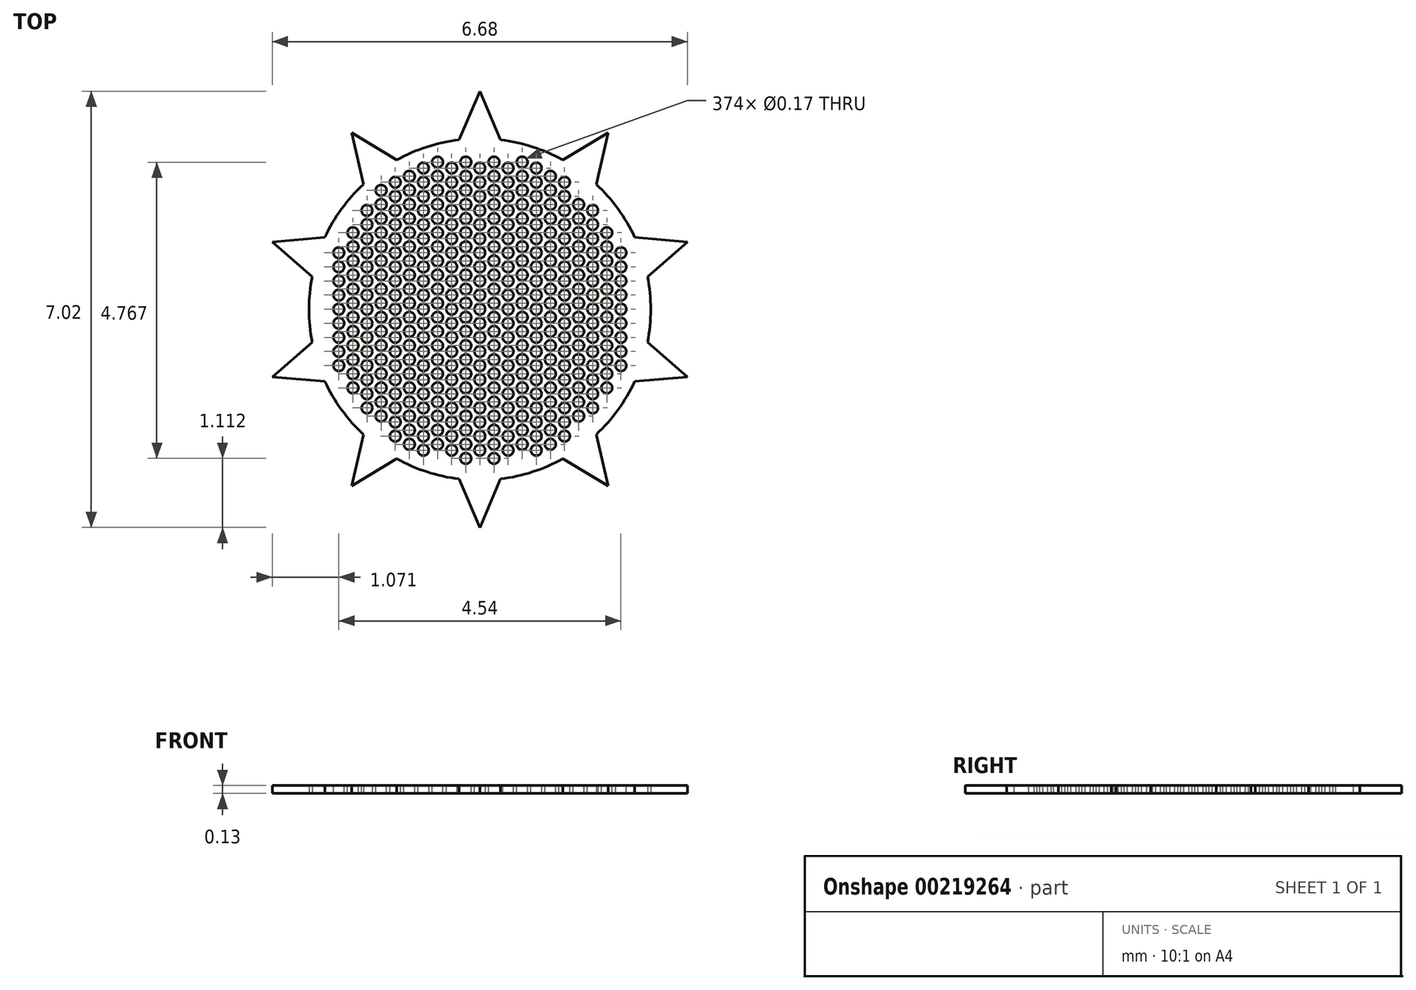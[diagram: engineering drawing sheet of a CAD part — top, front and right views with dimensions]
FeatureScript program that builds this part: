
annotation { "Feature Type Name" : "Feature", "Feature Type Description" : "" }
export const myFeature = defineFeature(function(context is Context, id is Id, definition is map)
    precondition{}
    {
        {
            var Q0;
            Q0=qCreatedBy(makeId("Top.planeOp"),FACE);
            var sketch = newSketch(context, id + "F0", { "sketchPlane" : qUnion([Q0])});
            skCircle(sketch, "E0", {"center": v(0, 0) * mm, "radius": 2.5 * mm});
            skCircle(sketch, "E1", {"center": v(0, 0) * mm, "radius": 2.75 * mm});
            skPoint(sketch, "E2", {"position": v(0, 2.75) * mm});
            skLineSegment(sketch, "E3", {"start": v(-3.94, 3.51) * mm, "end": v(3.7, 3.51) * mm, "construction": true});
            skLineSegment(sketch, "E4", {"start": v(0, 3.51) * mm, "end": v(-0.33, 2.73) * mm});
            skLineSegment(sketch, "E5", {"start": v(0, 3.51) * mm, "end": v(0.33, 2.73) * mm});
            skLineSegment(sketch, "E6.1.0", {"start": v(-2.06, 2.84) * mm, "end": v(-1.87, 2.01) * mm});
            skLineSegment(sketch, "E6.1.1", {"start": v(-2.06, 2.84) * mm, "end": v(-1.34, 2.4) * mm});
            skLineSegment(sketch, "E6.2.0", {"start": v(-3.34, 1.09) * mm, "end": v(-2.7, 0.53) * mm});
            skLineSegment(sketch, "E6.2.1", {"start": v(-3.34, 1.09) * mm, "end": v(-2.5, 1.16) * mm});
            skLineSegment(sketch, "E6.3.0", {"start": v(-3.34, -1.09) * mm, "end": v(-2.5, -1.16) * mm});
            skLineSegment(sketch, "E6.3.1", {"start": v(-3.34, -1.09) * mm, "end": v(-2.7, -0.53) * mm});
            skLineSegment(sketch, "E6.4.0", {"start": v(-2.06, -2.84) * mm, "end": v(-1.34, -2.4) * mm});
            skLineSegment(sketch, "E6.4.1", {"start": v(-2.06, -2.84) * mm, "end": v(-1.87, -2.01) * mm});
            skLineSegment(sketch, "E6.5.0", {"start": v(0, -3.51) * mm, "end": v(0.33, -2.73) * mm});
            skLineSegment(sketch, "E6.5.1", {"start": v(0, -3.51) * mm, "end": v(-0.33, -2.73) * mm});
            skLineSegment(sketch, "E6.6.0", {"start": v(2.06, -2.84) * mm, "end": v(1.87, -2.01) * mm});
            skLineSegment(sketch, "E6.6.1", {"start": v(2.06, -2.84) * mm, "end": v(1.34, -2.4) * mm});
            skLineSegment(sketch, "E6.7.0", {"start": v(3.34, -1.09) * mm, "end": v(2.7, -0.53) * mm});
            skLineSegment(sketch, "E6.7.1", {"start": v(3.34, -1.09) * mm, "end": v(2.5, -1.16) * mm});
            skLineSegment(sketch, "E6.8.0", {"start": v(3.34, 1.09) * mm, "end": v(2.5, 1.16) * mm});
            skLineSegment(sketch, "E6.8.1", {"start": v(3.34, 1.09) * mm, "end": v(2.7, 0.53) * mm});
            skLineSegment(sketch, "E6.9.0", {"start": v(2.06, 2.84) * mm, "end": v(1.34, 2.4) * mm});
            skLineSegment(sketch, "E6.9.1", {"start": v(2.06, 2.84) * mm, "end": v(1.87, 2.01) * mm});
            skSolve(sketch);
        }
        {
            var Q0;
            Q0=qSketchRegion(id+"F0",true);
            var Q1;
            Q1=makeQuery(id+"F0.imprint","IMPRINT",FACE,{"disambiguationData":[TD([[makeQuery(id+"F0.imprint","IMPRINT",EDGE,{"derivedFrom":sQuery(id+"F0.wireOp",EDGE,"E0")}),1.0]])]});
            extrude(context, id + "F1", {"entities" : qUnion([Q0, Q1]), "depth" : 0.13 * mm});
        }
        {
            var Q0;
            Q0=makeQuery(id+"F1.opExtrude","CAP_FACE",FACE,{"disambiguationData":[OSD([sQuery(id+"F0.wireOp",EDGE,"E1"),sQuery(id+"F0.wireOp",EDGE,"E4"),sQuery(id+"F0.wireOp",EDGE,"E5"),sQuery(id+"F0.wireOp",EDGE,"E6.1.0"),sQuery(id+"F0.wireOp",EDGE,"E6.1.1"),sQuery(id+"F0.wireOp",EDGE,"E6.2.0"),sQuery(id+"F0.wireOp",EDGE,"E6.2.1"),sQuery(id+"F0.wireOp",EDGE,"E6.3.0"),sQuery(id+"F0.wireOp",EDGE,"E6.3.1"),sQuery(id+"F0.wireOp",EDGE,"E6.4.0"),sQuery(id+"F0.wireOp",EDGE,"E6.4.1"),sQuery(id+"F0.wireOp",EDGE,"E6.5.0"),sQuery(id+"F0.wireOp",EDGE,"E6.5.1"),sQuery(id+"F0.wireOp",EDGE,"E6.6.0"),sQuery(id+"F0.wireOp",EDGE,"E6.6.1"),sQuery(id+"F0.wireOp",EDGE,"E6.7.0"),sQuery(id+"F0.wireOp",EDGE,"E6.7.1"),sQuery(id+"F0.wireOp",EDGE,"E6.8.0"),sQuery(id+"F0.wireOp",EDGE,"E6.8.1"),sQuery(id+"F0.wireOp",EDGE,"E6.9.0"),sQuery(id+"F0.wireOp",EDGE,"E6.9.1")])],"isStart":false});
            cPlane(context, id + "F2", {"entities" : qUnion([Q0]), "cplaneType" : CPlaneType.OFFSET, "offset" : 0 * mm, "width" : 150 * mm, "height" : 150 * mm});
        }
        {
            var Q0;
            Q0=qCreatedBy(id+"F2.planeOp",FACE);
            var sketch = newSketch(context, id + "F3", { "sketchPlane" : qUnion([Q0])});
            skCircle(sketch, "E7.2.1.8", {"center": v(-2.04, 1.23) * mm, "radius": 0.09 * mm});
            skCircle(sketch, "E7.2.1.9", {"center": v(-2.04, 1) * mm, "radius": 0.09 * mm});
            skCircle(sketch, "E7.0.1.10", {"center": v(-2.27, 0.91) * mm, "radius": 0.09 * mm});
            skCircle(sketch, "E7.2.1.10", {"center": v(-2.04, 0.78) * mm, "radius": 0.09 * mm});
            skCircle(sketch, "E7.2.2.5", {"center": v(-1.59, 1.91) * mm, "radius": 0.09 * mm});
            skCircle(sketch, "E7.2.2.6", {"center": v(-1.59, 1.69) * mm, "radius": 0.09 * mm});
            skCircle(sketch, "E7.0.2.7", {"center": v(-1.82, 1.6) * mm, "radius": 0.09 * mm});
            skCircle(sketch, "E7.2.2.7", {"center": v(-1.59, 1.46) * mm, "radius": 0.09 * mm});
            skCircle(sketch, "E7.0.2.8", {"center": v(-1.82, 1.36) * mm, "radius": 0.09 * mm});
            skCircle(sketch, "E7.2.2.8", {"center": v(-1.59, 1.23) * mm, "radius": 0.09 * mm});
            skCircle(sketch, "E7.0.2.9", {"center": v(-1.82, 1.14) * mm, "radius": 0.09 * mm});
            skCircle(sketch, "E7.2.2.9", {"center": v(-1.59, 1) * mm, "radius": 0.09 * mm});
            skCircle(sketch, "E7.0.2.10", {"center": v(-1.82, 0.91) * mm, "radius": 0.09 * mm});
            skCircle(sketch, "E7.2.2.10", {"center": v(-1.59, 0.78) * mm, "radius": 0.09 * mm});
            skCircle(sketch, "E7.2.3.4", {"center": v(-1.13, 2.14) * mm, "radius": 0.09 * mm});
            skCircle(sketch, "E7.0.3.5", {"center": v(-1.36, 2.05) * mm, "radius": 0.09 * mm});
            skCircle(sketch, "E7.2.3.5", {"center": v(-1.13, 1.91) * mm, "radius": 0.09 * mm});
            skCircle(sketch, "E7.0.3.6", {"center": v(-1.36, 1.82) * mm, "radius": 0.09 * mm});
            skCircle(sketch, "E7.2.3.6", {"center": v(-1.13, 1.69) * mm, "radius": 0.09 * mm});
            skCircle(sketch, "E7.0.3.7", {"center": v(-1.36, 1.6) * mm, "radius": 0.09 * mm});
            skCircle(sketch, "E7.2.3.7", {"center": v(-1.13, 1.46) * mm, "radius": 0.09 * mm});
            skCircle(sketch, "E7.0.3.8", {"center": v(-1.36, 1.36) * mm, "radius": 0.09 * mm});
            skCircle(sketch, "E7.2.3.8", {"center": v(-1.13, 1.23) * mm, "radius": 0.09 * mm});
            skCircle(sketch, "E7.0.3.9", {"center": v(-1.36, 1.14) * mm, "radius": 0.09 * mm});
            skCircle(sketch, "E7.2.3.9", {"center": v(-1.13, 1) * mm, "radius": 0.09 * mm});
            skCircle(sketch, "E7.0.3.10", {"center": v(-1.36, 0.91) * mm, "radius": 0.09 * mm});
            skCircle(sketch, "E7.2.3.10", {"center": v(-1.13, 0.78) * mm, "radius": 0.09 * mm});
            skCircle(sketch, "E7.2.4.3", {"center": v(-0.68, 2.37) * mm, "radius": 0.09 * mm});
            skCircle(sketch, "E7.0.4.4", {"center": v(-0.9, 2.27) * mm, "radius": 0.09 * mm});
            skCircle(sketch, "E7.2.4.4", {"center": v(-0.68, 2.14) * mm, "radius": 0.09 * mm});
            skCircle(sketch, "E7.0.4.5", {"center": v(-0.9, 2.05) * mm, "radius": 0.09 * mm});
            skCircle(sketch, "E7.2.4.5", {"center": v(-0.68, 1.91) * mm, "radius": 0.09 * mm});
            skCircle(sketch, "E7.0.4.6", {"center": v(-0.9, 1.82) * mm, "radius": 0.09 * mm});
            skCircle(sketch, "E7.2.4.6", {"center": v(-0.68, 1.69) * mm, "radius": 0.09 * mm});
            skCircle(sketch, "E7.0.4.7", {"center": v(-0.9, 1.6) * mm, "radius": 0.09 * mm});
            skCircle(sketch, "E7.2.4.7", {"center": v(-0.68, 1.46) * mm, "radius": 0.09 * mm});
            skCircle(sketch, "E7.0.4.8", {"center": v(-0.9, 1.36) * mm, "radius": 0.09 * mm});
            skCircle(sketch, "E7.2.4.8", {"center": v(-0.68, 1.23) * mm, "radius": 0.09 * mm});
            skCircle(sketch, "E7.0.4.9", {"center": v(-0.9, 1.14) * mm, "radius": 0.09 * mm});
            skCircle(sketch, "E7.2.4.9", {"center": v(-0.68, 1) * mm, "radius": 0.09 * mm});
            skCircle(sketch, "E7.0.4.10", {"center": v(-0.9, 0.91) * mm, "radius": 0.09 * mm});
            skCircle(sketch, "E7.2.4.10", {"center": v(-0.68, 0.78) * mm, "radius": 0.09 * mm});
            skCircle(sketch, "E7.2.5.3", {"center": v(-0.23, 2.37) * mm, "radius": 0.09 * mm});
            skCircle(sketch, "E7.0.5.4", {"center": v(-0.45, 2.27) * mm, "radius": 0.09 * mm});
            skCircle(sketch, "E7.2.5.4", {"center": v(-0.23, 2.14) * mm, "radius": 0.09 * mm});
            skCircle(sketch, "E7.0.5.5", {"center": v(-0.45, 2.05) * mm, "radius": 0.09 * mm});
            skCircle(sketch, "E7.2.5.5", {"center": v(-0.23, 1.91) * mm, "radius": 0.09 * mm});
            skCircle(sketch, "E7.0.5.6", {"center": v(-0.45, 1.82) * mm, "radius": 0.09 * mm});
            skCircle(sketch, "E7.2.5.6", {"center": v(-0.23, 1.69) * mm, "radius": 0.09 * mm});
            skCircle(sketch, "E7.0.5.7", {"center": v(-0.45, 1.6) * mm, "radius": 0.09 * mm});
            skCircle(sketch, "E7.2.5.7", {"center": v(-0.23, 1.46) * mm, "radius": 0.09 * mm});
            skCircle(sketch, "E7.0.5.8", {"center": v(-0.45, 1.36) * mm, "radius": 0.09 * mm});
            skCircle(sketch, "E7.2.5.8", {"center": v(-0.23, 1.23) * mm, "radius": 0.09 * mm});
            skCircle(sketch, "E7.0.5.9", {"center": v(-0.45, 1.14) * mm, "radius": 0.09 * mm});
            skCircle(sketch, "E7.2.5.9", {"center": v(-0.23, 1) * mm, "radius": 0.09 * mm});
            skCircle(sketch, "E7.0.5.10", {"center": v(-0.45, 0.91) * mm, "radius": 0.09 * mm});
            skCircle(sketch, "E7.2.5.10", {"center": v(-0.23, 0.78) * mm, "radius": 0.09 * mm});
            skCircle(sketch, "E7.2.6.3", {"center": v(0.23, 2.37) * mm, "radius": 0.09 * mm});
            skCircle(sketch, "E7.0.6.4", {"center": v(0, 2.27) * mm, "radius": 0.09 * mm});
            skCircle(sketch, "E7.2.6.4", {"center": v(0.23, 2.14) * mm, "radius": 0.09 * mm});
            skCircle(sketch, "E7.0.6.5", {"center": v(0, 2.05) * mm, "radius": 0.09 * mm});
            skCircle(sketch, "E7.2.6.5", {"center": v(0.23, 1.91) * mm, "radius": 0.09 * mm});
            skCircle(sketch, "E7.0.6.6", {"center": v(0, 1.82) * mm, "radius": 0.09 * mm});
            skCircle(sketch, "E7.2.6.6", {"center": v(0.23, 1.69) * mm, "radius": 0.09 * mm});
            skCircle(sketch, "E7.0.6.7", {"center": v(0, 1.6) * mm, "radius": 0.09 * mm});
            skCircle(sketch, "E7.2.6.7", {"center": v(0.23, 1.46) * mm, "radius": 0.09 * mm});
            skCircle(sketch, "E7.0.6.8", {"center": v(0, 1.36) * mm, "radius": 0.09 * mm});
            skCircle(sketch, "E7.2.6.8", {"center": v(0.23, 1.23) * mm, "radius": 0.09 * mm});
            skCircle(sketch, "E7.0.6.9", {"center": v(0, 1.14) * mm, "radius": 0.09 * mm});
            skCircle(sketch, "E7.2.6.9", {"center": v(0.23, 1) * mm, "radius": 0.09 * mm});
            skCircle(sketch, "E7.0.6.10", {"center": v(0, 0.91) * mm, "radius": 0.09 * mm});
            skCircle(sketch, "E7.2.6.10", {"center": v(0.23, 0.78) * mm, "radius": 0.09 * mm});
            skCircle(sketch, "E7.2.7.3", {"center": v(0.68, 2.37) * mm, "radius": 0.09 * mm});
            skCircle(sketch, "E7.0.7.4", {"center": v(0.45, 2.27) * mm, "radius": 0.09 * mm});
            skCircle(sketch, "E7.2.7.4", {"center": v(0.68, 2.14) * mm, "radius": 0.09 * mm});
            skCircle(sketch, "E7.0.7.5", {"center": v(0.45, 2.05) * mm, "radius": 0.09 * mm});
            skCircle(sketch, "E7.2.7.5", {"center": v(0.68, 1.91) * mm, "radius": 0.09 * mm});
            skCircle(sketch, "E7.0.7.6", {"center": v(0.45, 1.82) * mm, "radius": 0.09 * mm});
            skCircle(sketch, "E7.2.7.6", {"center": v(0.68, 1.69) * mm, "radius": 0.09 * mm});
            skCircle(sketch, "E7.0.7.7", {"center": v(0.45, 1.6) * mm, "radius": 0.09 * mm});
            skCircle(sketch, "E7.2.7.7", {"center": v(0.68, 1.46) * mm, "radius": 0.09 * mm});
            skCircle(sketch, "E7.0.7.8", {"center": v(0.45, 1.36) * mm, "radius": 0.09 * mm});
            skCircle(sketch, "E7.2.7.8", {"center": v(0.68, 1.23) * mm, "radius": 0.09 * mm});
            skCircle(sketch, "E7.0.7.9", {"center": v(0.45, 1.14) * mm, "radius": 0.09 * mm});
            skCircle(sketch, "E7.2.7.9", {"center": v(0.68, 1) * mm, "radius": 0.09 * mm});
            skCircle(sketch, "E7.0.7.10", {"center": v(0.45, 0.91) * mm, "radius": 0.09 * mm});
            skCircle(sketch, "E7.2.7.10", {"center": v(0.68, 0.78) * mm, "radius": 0.09 * mm});
            skCircle(sketch, "E7.0.8.4", {"center": v(0.9, 2.27) * mm, "radius": 0.09 * mm});
            skCircle(sketch, "E7.2.8.4", {"center": v(1.14, 2.14) * mm, "radius": 0.09 * mm});
            skCircle(sketch, "E7.0.8.5", {"center": v(0.9, 2.05) * mm, "radius": 0.09 * mm});
            skCircle(sketch, "E7.2.8.5", {"center": v(1.14, 1.91) * mm, "radius": 0.09 * mm});
            skCircle(sketch, "E7.0.8.6", {"center": v(0.9, 1.82) * mm, "radius": 0.09 * mm});
            skCircle(sketch, "E7.2.8.6", {"center": v(1.14, 1.69) * mm, "radius": 0.09 * mm});
            skCircle(sketch, "E7.0.8.7", {"center": v(0.9, 1.6) * mm, "radius": 0.09 * mm});
            skCircle(sketch, "E7.2.8.7", {"center": v(1.14, 1.46) * mm, "radius": 0.09 * mm});
            skCircle(sketch, "E7.0.8.8", {"center": v(0.9, 1.36) * mm, "radius": 0.09 * mm});
            skCircle(sketch, "E7.2.8.8", {"center": v(1.14, 1.23) * mm, "radius": 0.09 * mm});
            skCircle(sketch, "E7.0.8.9", {"center": v(0.9, 1.14) * mm, "radius": 0.09 * mm});
            skCircle(sketch, "E7.2.8.9", {"center": v(1.14, 1) * mm, "radius": 0.09 * mm});
            skCircle(sketch, "E7.0.8.10", {"center": v(0.9, 0.91) * mm, "radius": 0.09 * mm});
            skCircle(sketch, "E7.2.8.10", {"center": v(1.14, 0.78) * mm, "radius": 0.09 * mm});
            skCircle(sketch, "E7.0.9.5", {"center": v(1.36, 2.05) * mm, "radius": 0.09 * mm});
            skCircle(sketch, "E7.0.9.6", {"center": v(1.36, 1.82) * mm, "radius": 0.09 * mm});
            skCircle(sketch, "E7.2.9.6", {"center": v(1.6, 1.69) * mm, "radius": 0.09 * mm});
            skCircle(sketch, "E7.0.9.7", {"center": v(1.36, 1.6) * mm, "radius": 0.09 * mm});
            skCircle(sketch, "E7.2.9.7", {"center": v(1.6, 1.46) * mm, "radius": 0.09 * mm});
            skCircle(sketch, "E7.0.9.8", {"center": v(1.36, 1.36) * mm, "radius": 0.09 * mm});
            skCircle(sketch, "E7.2.9.8", {"center": v(1.6, 1.23) * mm, "radius": 0.09 * mm});
            skCircle(sketch, "E7.0.9.9", {"center": v(1.36, 1.14) * mm, "radius": 0.09 * mm});
            skCircle(sketch, "E7.2.9.9", {"center": v(1.6, 1) * mm, "radius": 0.09 * mm});
            skCircle(sketch, "E7.0.9.10", {"center": v(1.36, 0.91) * mm, "radius": 0.09 * mm});
            skCircle(sketch, "E7.2.9.10", {"center": v(1.6, 0.78) * mm, "radius": 0.09 * mm});
            skCircle(sketch, "E7.0.10.7", {"center": v(1.82, 1.6) * mm, "radius": 0.09 * mm});
            skCircle(sketch, "E7.0.10.8", {"center": v(1.82, 1.36) * mm, "radius": 0.09 * mm});
            skCircle(sketch, "E7.2.10.8", {"center": v(2.04, 1.23) * mm, "radius": 0.09 * mm});
            skCircle(sketch, "E7.0.10.9", {"center": v(1.82, 1.14) * mm, "radius": 0.09 * mm});
            skCircle(sketch, "E7.2.10.9", {"center": v(2.04, 1) * mm, "radius": 0.09 * mm});
            skCircle(sketch, "E7.0.10.10", {"center": v(1.82, 0.91) * mm, "radius": 0.09 * mm});
            skCircle(sketch, "E7.2.10.10", {"center": v(2.04, 0.78) * mm, "radius": 0.09 * mm});
            skCircle(sketch, "E8.0.1.11", {"center": v(-2.27, 0.68) * mm, "radius": 0.09 * mm});
            skCircle(sketch, "E8.2.1.11", {"center": v(-2.04, 0.55) * mm, "radius": 0.09 * mm});
            skCircle(sketch, "E8.0.1.12", {"center": v(-2.27, 0.46) * mm, "radius": 0.09 * mm});
            skCircle(sketch, "E8.2.1.12", {"center": v(-2.04, 0.33) * mm, "radius": 0.09 * mm});
            skCircle(sketch, "E8.0.1.13", {"center": v(-2.27, 0.23) * mm, "radius": 0.09 * mm});
            skCircle(sketch, "E8.2.1.13", {"center": v(-2.04, 0.1) * mm, "radius": 0.09 * mm});
            skCircle(sketch, "E8.0.1.14", {"center": v(-2.27, 0) * mm, "radius": 0.09 * mm});
            skCircle(sketch, "E8.2.1.14", {"center": v(-2.04, -0.13) * mm, "radius": 0.09 * mm});
            skCircle(sketch, "E8.0.1.15", {"center": v(-2.27, -0.22) * mm, "radius": 0.09 * mm});
            skCircle(sketch, "E8.2.1.15", {"center": v(-2.04, -0.36) * mm, "radius": 0.09 * mm});
            skCircle(sketch, "E8.0.1.16", {"center": v(-2.27, -0.45) * mm, "radius": 0.09 * mm});
            skCircle(sketch, "E8.2.1.16", {"center": v(-2.04, -0.58) * mm, "radius": 0.09 * mm});
            skCircle(sketch, "E8.0.1.17", {"center": v(-2.27, -0.68) * mm, "radius": 0.09 * mm});
            skCircle(sketch, "E8.2.1.17", {"center": v(-2.04, -0.8) * mm, "radius": 0.09 * mm});
            skCircle(sketch, "E8.0.1.18", {"center": v(-2.27, -0.9) * mm, "radius": 0.09 * mm});
            skCircle(sketch, "E8.2.1.18", {"center": v(-2.04, -1.04) * mm, "radius": 0.09 * mm});
            skCircle(sketch, "E8.2.1.19", {"center": v(-2.04, -1.26) * mm, "radius": 0.09 * mm});
            skCircle(sketch, "E8.0.2.11", {"center": v(-1.82, 0.68) * mm, "radius": 0.09 * mm});
            skCircle(sketch, "E8.2.2.11", {"center": v(-1.59, 0.55) * mm, "radius": 0.09 * mm});
            skCircle(sketch, "E8.0.2.12", {"center": v(-1.82, 0.46) * mm, "radius": 0.09 * mm});
            skCircle(sketch, "E8.2.2.12", {"center": v(-1.59, 0.33) * mm, "radius": 0.09 * mm});
            skCircle(sketch, "E8.0.2.13", {"center": v(-1.82, 0.23) * mm, "radius": 0.09 * mm});
            skCircle(sketch, "E8.2.2.13", {"center": v(-1.59, 0.1) * mm, "radius": 0.09 * mm});
            skCircle(sketch, "E8.0.2.14", {"center": v(-1.82, 0) * mm, "radius": 0.09 * mm});
            skCircle(sketch, "E8.2.2.14", {"center": v(-1.59, -0.13) * mm, "radius": 0.09 * mm});
            skCircle(sketch, "E8.0.2.15", {"center": v(-1.82, -0.22) * mm, "radius": 0.09 * mm});
            skCircle(sketch, "E8.2.2.15", {"center": v(-1.59, -0.36) * mm, "radius": 0.09 * mm});
            skCircle(sketch, "E8.0.2.16", {"center": v(-1.82, -0.45) * mm, "radius": 0.09 * mm});
            skCircle(sketch, "E8.2.2.16", {"center": v(-1.59, -0.58) * mm, "radius": 0.09 * mm});
            skCircle(sketch, "E8.0.2.17", {"center": v(-1.82, -0.68) * mm, "radius": 0.09 * mm});
            skCircle(sketch, "E8.2.2.17", {"center": v(-1.59, -0.8) * mm, "radius": 0.09 * mm});
            skCircle(sketch, "E8.0.2.18", {"center": v(-1.82, -0.9) * mm, "radius": 0.09 * mm});
            skCircle(sketch, "E8.2.2.18", {"center": v(-1.59, -1.04) * mm, "radius": 0.09 * mm});
            skCircle(sketch, "E8.0.2.19", {"center": v(-1.82, -1.13) * mm, "radius": 0.09 * mm});
            skCircle(sketch, "E8.2.2.19", {"center": v(-1.59, -1.26) * mm, "radius": 0.09 * mm});
            skCircle(sketch, "E8.0.2.20", {"center": v(-1.82, -1.36) * mm, "radius": 0.09 * mm});
            skCircle(sketch, "E8.2.2.20", {"center": v(-1.59, -1.5) * mm, "radius": 0.09 * mm});
            skCircle(sketch, "E8.0.2.21", {"center": v(-1.82, -1.59) * mm, "radius": 0.09 * mm});
            skCircle(sketch, "E8.2.2.21", {"center": v(-1.59, -1.72) * mm, "radius": 0.09 * mm});
            skCircle(sketch, "E8.0.3.11", {"center": v(-1.36, 0.68) * mm, "radius": 0.09 * mm});
            skCircle(sketch, "E8.2.3.11", {"center": v(-1.13, 0.55) * mm, "radius": 0.09 * mm});
            skCircle(sketch, "E8.0.3.12", {"center": v(-1.36, 0.46) * mm, "radius": 0.09 * mm});
            skCircle(sketch, "E8.2.3.12", {"center": v(-1.13, 0.33) * mm, "radius": 0.09 * mm});
            skCircle(sketch, "E8.0.3.13", {"center": v(-1.36, 0.23) * mm, "radius": 0.09 * mm});
            skCircle(sketch, "E8.2.3.13", {"center": v(-1.13, 0.1) * mm, "radius": 0.09 * mm});
            skCircle(sketch, "E8.0.3.14", {"center": v(-1.36, 0) * mm, "radius": 0.09 * mm});
            skCircle(sketch, "E8.2.3.14", {"center": v(-1.13, -0.13) * mm, "radius": 0.09 * mm});
            skCircle(sketch, "E8.0.3.15", {"center": v(-1.36, -0.22) * mm, "radius": 0.09 * mm});
            skCircle(sketch, "E8.2.3.15", {"center": v(-1.13, -0.36) * mm, "radius": 0.09 * mm});
            skCircle(sketch, "E8.0.3.16", {"center": v(-1.36, -0.45) * mm, "radius": 0.09 * mm});
            skCircle(sketch, "E8.2.3.16", {"center": v(-1.13, -0.58) * mm, "radius": 0.09 * mm});
            skCircle(sketch, "E8.0.3.17", {"center": v(-1.36, -0.68) * mm, "radius": 0.09 * mm});
            skCircle(sketch, "E8.2.3.17", {"center": v(-1.13, -0.8) * mm, "radius": 0.09 * mm});
            skCircle(sketch, "E8.0.3.18", {"center": v(-1.36, -0.9) * mm, "radius": 0.09 * mm});
            skCircle(sketch, "E8.2.3.18", {"center": v(-1.13, -1.04) * mm, "radius": 0.09 * mm});
            skCircle(sketch, "E8.0.3.19", {"center": v(-1.36, -1.13) * mm, "radius": 0.09 * mm});
            skCircle(sketch, "E8.2.3.19", {"center": v(-1.13, -1.26) * mm, "radius": 0.09 * mm});
            skCircle(sketch, "E8.0.3.20", {"center": v(-1.36, -1.36) * mm, "radius": 0.09 * mm});
            skCircle(sketch, "E8.2.3.20", {"center": v(-1.13, -1.5) * mm, "radius": 0.09 * mm});
            skCircle(sketch, "E8.0.3.21", {"center": v(-1.36, -1.59) * mm, "radius": 0.09 * mm});
            skCircle(sketch, "E8.2.3.21", {"center": v(-1.13, -1.72) * mm, "radius": 0.09 * mm});
            skCircle(sketch, "E8.0.4.11", {"center": v(-0.9, 0.68) * mm, "radius": 0.09 * mm});
            skCircle(sketch, "E8.2.4.11", {"center": v(-0.68, 0.55) * mm, "radius": 0.09 * mm});
            skCircle(sketch, "E8.0.4.12", {"center": v(-0.9, 0.46) * mm, "radius": 0.09 * mm});
            skCircle(sketch, "E8.2.4.12", {"center": v(-0.68, 0.33) * mm, "radius": 0.09 * mm});
            skCircle(sketch, "E8.0.4.13", {"center": v(-0.9, 0.23) * mm, "radius": 0.09 * mm});
            skCircle(sketch, "E8.2.4.13", {"center": v(-0.68, 0.1) * mm, "radius": 0.09 * mm});
            skCircle(sketch, "E8.0.4.14", {"center": v(-0.9, 0) * mm, "radius": 0.09 * mm});
            skCircle(sketch, "E8.2.4.14", {"center": v(-0.68, -0.13) * mm, "radius": 0.09 * mm});
            skCircle(sketch, "E8.0.4.15", {"center": v(-0.9, -0.22) * mm, "radius": 0.09 * mm});
            skCircle(sketch, "E8.2.4.15", {"center": v(-0.68, -0.36) * mm, "radius": 0.09 * mm});
            skCircle(sketch, "E8.0.4.16", {"center": v(-0.9, -0.45) * mm, "radius": 0.09 * mm});
            skCircle(sketch, "E8.2.4.16", {"center": v(-0.68, -0.58) * mm, "radius": 0.09 * mm});
            skCircle(sketch, "E8.0.4.17", {"center": v(-0.9, -0.68) * mm, "radius": 0.09 * mm});
            skCircle(sketch, "E8.2.4.17", {"center": v(-0.68, -0.8) * mm, "radius": 0.09 * mm});
            skCircle(sketch, "E8.0.4.18", {"center": v(-0.9, -0.9) * mm, "radius": 0.09 * mm});
            skCircle(sketch, "E8.2.4.18", {"center": v(-0.68, -1.04) * mm, "radius": 0.09 * mm});
            skCircle(sketch, "E8.0.4.19", {"center": v(-0.9, -1.13) * mm, "radius": 0.09 * mm});
            skCircle(sketch, "E8.2.4.19", {"center": v(-0.68, -1.26) * mm, "radius": 0.09 * mm});
            skCircle(sketch, "E8.0.4.20", {"center": v(-0.9, -1.36) * mm, "radius": 0.09 * mm});
            skCircle(sketch, "E8.2.4.20", {"center": v(-0.68, -1.5) * mm, "radius": 0.09 * mm});
            skCircle(sketch, "E8.0.4.21", {"center": v(-0.9, -1.59) * mm, "radius": 0.09 * mm});
            skCircle(sketch, "E8.2.4.21", {"center": v(-0.68, -1.72) * mm, "radius": 0.09 * mm});
            skCircle(sketch, "E8.0.5.11", {"center": v(-0.45, 0.68) * mm, "radius": 0.09 * mm});
            skCircle(sketch, "E8.2.5.11", {"center": v(-0.23, 0.55) * mm, "radius": 0.09 * mm});
            skCircle(sketch, "E8.0.5.12", {"center": v(-0.45, 0.46) * mm, "radius": 0.09 * mm});
            skCircle(sketch, "E8.2.5.12", {"center": v(-0.23, 0.33) * mm, "radius": 0.09 * mm});
            skCircle(sketch, "E8.0.5.13", {"center": v(-0.45, 0.23) * mm, "radius": 0.09 * mm});
            skCircle(sketch, "E8.2.5.13", {"center": v(-0.23, 0.1) * mm, "radius": 0.09 * mm});
            skCircle(sketch, "E8.0.5.14", {"center": v(-0.45, 0) * mm, "radius": 0.09 * mm});
            skCircle(sketch, "E8.2.5.14", {"center": v(-0.23, -0.13) * mm, "radius": 0.09 * mm});
            skCircle(sketch, "E8.0.5.15", {"center": v(-0.45, -0.22) * mm, "radius": 0.09 * mm});
            skCircle(sketch, "E8.2.5.15", {"center": v(-0.23, -0.36) * mm, "radius": 0.09 * mm});
            skCircle(sketch, "E8.0.5.16", {"center": v(-0.45, -0.45) * mm, "radius": 0.09 * mm});
            skCircle(sketch, "E8.2.5.16", {"center": v(-0.23, -0.58) * mm, "radius": 0.09 * mm});
            skCircle(sketch, "E8.0.5.17", {"center": v(-0.45, -0.68) * mm, "radius": 0.09 * mm});
            skCircle(sketch, "E8.2.5.17", {"center": v(-0.23, -0.8) * mm, "radius": 0.09 * mm});
            skCircle(sketch, "E8.0.5.18", {"center": v(-0.45, -0.9) * mm, "radius": 0.09 * mm});
            skCircle(sketch, "E8.2.5.18", {"center": v(-0.23, -1.04) * mm, "radius": 0.09 * mm});
            skCircle(sketch, "E8.0.5.19", {"center": v(-0.45, -1.13) * mm, "radius": 0.09 * mm});
            skCircle(sketch, "E8.2.5.19", {"center": v(-0.23, -1.26) * mm, "radius": 0.09 * mm});
            skCircle(sketch, "E8.0.5.20", {"center": v(-0.45, -1.36) * mm, "radius": 0.09 * mm});
            skCircle(sketch, "E8.2.5.20", {"center": v(-0.23, -1.5) * mm, "radius": 0.09 * mm});
            skCircle(sketch, "E8.0.5.21", {"center": v(-0.45, -1.59) * mm, "radius": 0.09 * mm});
            skCircle(sketch, "E8.2.5.21", {"center": v(-0.23, -1.72) * mm, "radius": 0.09 * mm});
            skCircle(sketch, "E8.0.6.11", {"center": v(0, 0.68) * mm, "radius": 0.09 * mm});
            skCircle(sketch, "E8.2.6.11", {"center": v(0.23, 0.55) * mm, "radius": 0.09 * mm});
            skCircle(sketch, "E8.0.6.12", {"center": v(0, 0.46) * mm, "radius": 0.09 * mm});
            skCircle(sketch, "E8.2.6.12", {"center": v(0.23, 0.33) * mm, "radius": 0.09 * mm});
            skCircle(sketch, "E8.0.6.13", {"center": v(0, 0.23) * mm, "radius": 0.09 * mm});
            skCircle(sketch, "E8.2.6.13", {"center": v(0.23, 0.1) * mm, "radius": 0.09 * mm});
            skCircle(sketch, "E8.0.6.14", {"center": v(0, 0) * mm, "radius": 0.09 * mm});
            skCircle(sketch, "E8.2.6.14", {"center": v(0.23, -0.13) * mm, "radius": 0.09 * mm});
            skCircle(sketch, "E8.0.6.15", {"center": v(0, -0.22) * mm, "radius": 0.09 * mm});
            skCircle(sketch, "E8.2.6.15", {"center": v(0.23, -0.36) * mm, "radius": 0.09 * mm});
            skCircle(sketch, "E8.0.6.16", {"center": v(0, -0.45) * mm, "radius": 0.09 * mm});
            skCircle(sketch, "E8.2.6.16", {"center": v(0.23, -0.58) * mm, "radius": 0.09 * mm});
            skCircle(sketch, "E8.0.6.17", {"center": v(0, -0.68) * mm, "radius": 0.09 * mm});
            skCircle(sketch, "E8.2.6.17", {"center": v(0.23, -0.8) * mm, "radius": 0.09 * mm});
            skCircle(sketch, "E8.0.6.18", {"center": v(0, -0.9) * mm, "radius": 0.09 * mm});
            skCircle(sketch, "E8.2.6.18", {"center": v(0.23, -1.04) * mm, "radius": 0.09 * mm});
            skCircle(sketch, "E8.0.6.19", {"center": v(0, -1.13) * mm, "radius": 0.09 * mm});
            skCircle(sketch, "E8.2.6.19", {"center": v(0.23, -1.26) * mm, "radius": 0.09 * mm});
            skCircle(sketch, "E8.0.6.20", {"center": v(0, -1.36) * mm, "radius": 0.09 * mm});
            skCircle(sketch, "E8.2.6.20", {"center": v(0.23, -1.5) * mm, "radius": 0.09 * mm});
            skCircle(sketch, "E8.0.6.21", {"center": v(0, -1.59) * mm, "radius": 0.09 * mm});
            skCircle(sketch, "E8.2.6.21", {"center": v(0.23, -1.72) * mm, "radius": 0.09 * mm});
            skCircle(sketch, "E8.0.7.11", {"center": v(0.45, 0.68) * mm, "radius": 0.09 * mm});
            skCircle(sketch, "E8.2.7.11", {"center": v(0.68, 0.55) * mm, "radius": 0.09 * mm});
            skCircle(sketch, "E8.0.7.12", {"center": v(0.45, 0.46) * mm, "radius": 0.09 * mm});
            skCircle(sketch, "E8.2.7.12", {"center": v(0.68, 0.33) * mm, "radius": 0.09 * mm});
            skCircle(sketch, "E8.0.7.13", {"center": v(0.45, 0.23) * mm, "radius": 0.09 * mm});
            skCircle(sketch, "E8.2.7.13", {"center": v(0.68, 0.1) * mm, "radius": 0.09 * mm});
            skCircle(sketch, "E8.0.7.14", {"center": v(0.45, 0) * mm, "radius": 0.09 * mm});
            skCircle(sketch, "E8.2.7.14", {"center": v(0.68, -0.13) * mm, "radius": 0.09 * mm});
            skCircle(sketch, "E8.0.7.15", {"center": v(0.45, -0.22) * mm, "radius": 0.09 * mm});
            skCircle(sketch, "E8.2.7.15", {"center": v(0.68, -0.36) * mm, "radius": 0.09 * mm});
            skCircle(sketch, "E8.0.7.16", {"center": v(0.45, -0.45) * mm, "radius": 0.09 * mm});
            skCircle(sketch, "E8.2.7.16", {"center": v(0.68, -0.58) * mm, "radius": 0.09 * mm});
            skCircle(sketch, "E8.0.7.17", {"center": v(0.45, -0.68) * mm, "radius": 0.09 * mm});
            skCircle(sketch, "E8.2.7.17", {"center": v(0.68, -0.8) * mm, "radius": 0.09 * mm});
            skCircle(sketch, "E8.0.7.18", {"center": v(0.45, -0.9) * mm, "radius": 0.09 * mm});
            skCircle(sketch, "E8.2.7.18", {"center": v(0.68, -1.04) * mm, "radius": 0.09 * mm});
            skCircle(sketch, "E8.0.7.19", {"center": v(0.45, -1.13) * mm, "radius": 0.09 * mm});
            skCircle(sketch, "E8.2.7.19", {"center": v(0.68, -1.26) * mm, "radius": 0.09 * mm});
            skCircle(sketch, "E8.0.7.20", {"center": v(0.45, -1.36) * mm, "radius": 0.09 * mm});
            skCircle(sketch, "E8.2.7.20", {"center": v(0.68, -1.5) * mm, "radius": 0.09 * mm});
            skCircle(sketch, "E8.0.7.21", {"center": v(0.45, -1.59) * mm, "radius": 0.09 * mm});
            skCircle(sketch, "E8.2.7.21", {"center": v(0.68, -1.72) * mm, "radius": 0.09 * mm});
            skCircle(sketch, "E8.0.8.11", {"center": v(0.9, 0.68) * mm, "radius": 0.09 * mm});
            skCircle(sketch, "E8.2.8.11", {"center": v(1.14, 0.55) * mm, "radius": 0.09 * mm});
            skCircle(sketch, "E8.0.8.12", {"center": v(0.9, 0.46) * mm, "radius": 0.09 * mm});
            skCircle(sketch, "E8.2.8.12", {"center": v(1.14, 0.33) * mm, "radius": 0.09 * mm});
            skCircle(sketch, "E8.0.8.13", {"center": v(0.9, 0.23) * mm, "radius": 0.09 * mm});
            skCircle(sketch, "E8.2.8.13", {"center": v(1.14, 0.1) * mm, "radius": 0.09 * mm});
            skCircle(sketch, "E8.0.8.14", {"center": v(0.9, 0) * mm, "radius": 0.09 * mm});
            skCircle(sketch, "E8.2.8.14", {"center": v(1.14, -0.13) * mm, "radius": 0.09 * mm});
            skCircle(sketch, "E8.0.8.15", {"center": v(0.9, -0.22) * mm, "radius": 0.09 * mm});
            skCircle(sketch, "E8.2.8.15", {"center": v(1.14, -0.36) * mm, "radius": 0.09 * mm});
            skCircle(sketch, "E8.0.8.16", {"center": v(0.9, -0.45) * mm, "radius": 0.09 * mm});
            skCircle(sketch, "E8.2.8.16", {"center": v(1.14, -0.58) * mm, "radius": 0.09 * mm});
            skCircle(sketch, "E8.0.8.17", {"center": v(0.9, -0.68) * mm, "radius": 0.09 * mm});
            skCircle(sketch, "E8.2.8.17", {"center": v(1.14, -0.8) * mm, "radius": 0.09 * mm});
            skCircle(sketch, "E8.0.8.18", {"center": v(0.9, -0.9) * mm, "radius": 0.09 * mm});
            skCircle(sketch, "E8.2.8.18", {"center": v(1.14, -1.04) * mm, "radius": 0.09 * mm});
            skCircle(sketch, "E8.0.8.19", {"center": v(0.9, -1.13) * mm, "radius": 0.09 * mm});
            skCircle(sketch, "E8.2.8.19", {"center": v(1.14, -1.26) * mm, "radius": 0.09 * mm});
            skCircle(sketch, "E8.0.8.20", {"center": v(0.9, -1.36) * mm, "radius": 0.09 * mm});
            skCircle(sketch, "E8.2.8.20", {"center": v(1.14, -1.5) * mm, "radius": 0.09 * mm});
            skCircle(sketch, "E8.0.8.21", {"center": v(0.9, -1.59) * mm, "radius": 0.09 * mm});
            skCircle(sketch, "E8.2.8.21", {"center": v(1.14, -1.72) * mm, "radius": 0.09 * mm});
            skCircle(sketch, "E8.0.9.11", {"center": v(1.36, 0.68) * mm, "radius": 0.09 * mm});
            skCircle(sketch, "E8.2.9.11", {"center": v(1.6, 0.55) * mm, "radius": 0.09 * mm});
            skCircle(sketch, "E8.0.9.12", {"center": v(1.36, 0.46) * mm, "radius": 0.09 * mm});
            skCircle(sketch, "E8.2.9.12", {"center": v(1.6, 0.33) * mm, "radius": 0.09 * mm});
            skCircle(sketch, "E8.0.9.13", {"center": v(1.36, 0.23) * mm, "radius": 0.09 * mm});
            skCircle(sketch, "E8.2.9.13", {"center": v(1.6, 0.1) * mm, "radius": 0.09 * mm});
            skCircle(sketch, "E8.0.9.14", {"center": v(1.36, 0) * mm, "radius": 0.09 * mm});
            skCircle(sketch, "E8.2.9.14", {"center": v(1.6, -0.13) * mm, "radius": 0.09 * mm});
            skCircle(sketch, "E8.0.9.15", {"center": v(1.36, -0.22) * mm, "radius": 0.09 * mm});
            skCircle(sketch, "E8.2.9.15", {"center": v(1.6, -0.36) * mm, "radius": 0.09 * mm});
            skCircle(sketch, "E8.0.9.16", {"center": v(1.36, -0.45) * mm, "radius": 0.09 * mm});
            skCircle(sketch, "E8.2.9.16", {"center": v(1.6, -0.58) * mm, "radius": 0.09 * mm});
            skCircle(sketch, "E8.0.9.17", {"center": v(1.36, -0.68) * mm, "radius": 0.09 * mm});
            skCircle(sketch, "E8.2.9.17", {"center": v(1.6, -0.8) * mm, "radius": 0.09 * mm});
            skCircle(sketch, "E8.0.9.18", {"center": v(1.36, -0.9) * mm, "radius": 0.09 * mm});
            skCircle(sketch, "E8.2.9.18", {"center": v(1.6, -1.04) * mm, "radius": 0.09 * mm});
            skCircle(sketch, "E8.0.9.19", {"center": v(1.36, -1.13) * mm, "radius": 0.09 * mm});
            skCircle(sketch, "E8.2.9.19", {"center": v(1.6, -1.26) * mm, "radius": 0.09 * mm});
            skCircle(sketch, "E8.0.9.20", {"center": v(1.36, -1.36) * mm, "radius": 0.09 * mm});
            skCircle(sketch, "E8.2.9.20", {"center": v(1.6, -1.5) * mm, "radius": 0.09 * mm});
            skCircle(sketch, "E8.0.9.21", {"center": v(1.36, -1.59) * mm, "radius": 0.09 * mm});
            skCircle(sketch, "E8.2.9.21", {"center": v(1.6, -1.72) * mm, "radius": 0.09 * mm});
            skCircle(sketch, "E8.0.10.11", {"center": v(1.82, 0.68) * mm, "radius": 0.09 * mm});
            skCircle(sketch, "E8.2.10.11", {"center": v(2.04, 0.55) * mm, "radius": 0.09 * mm});
            skCircle(sketch, "E8.0.10.12", {"center": v(1.82, 0.46) * mm, "radius": 0.09 * mm});
            skCircle(sketch, "E8.2.10.12", {"center": v(2.04, 0.33) * mm, "radius": 0.09 * mm});
            skCircle(sketch, "E8.0.10.13", {"center": v(1.82, 0.23) * mm, "radius": 0.09 * mm});
            skCircle(sketch, "E8.2.10.13", {"center": v(2.04, 0.1) * mm, "radius": 0.09 * mm});
            skCircle(sketch, "E8.0.10.14", {"center": v(1.82, 0) * mm, "radius": 0.09 * mm});
            skCircle(sketch, "E8.2.10.14", {"center": v(2.04, -0.13) * mm, "radius": 0.09 * mm});
            skCircle(sketch, "E8.0.10.15", {"center": v(1.82, -0.22) * mm, "radius": 0.09 * mm});
            skCircle(sketch, "E8.2.10.15", {"center": v(2.04, -0.36) * mm, "radius": 0.09 * mm});
            skCircle(sketch, "E8.0.10.16", {"center": v(1.82, -0.45) * mm, "radius": 0.09 * mm});
            skCircle(sketch, "E8.2.10.16", {"center": v(2.04, -0.58) * mm, "radius": 0.09 * mm});
            skCircle(sketch, "E8.0.10.17", {"center": v(1.82, -0.68) * mm, "radius": 0.09 * mm});
            skCircle(sketch, "E8.2.10.17", {"center": v(2.04, -0.8) * mm, "radius": 0.09 * mm});
            skCircle(sketch, "E8.0.10.18", {"center": v(1.82, -0.9) * mm, "radius": 0.09 * mm});
            skCircle(sketch, "E8.2.10.18", {"center": v(2.04, -1.04) * mm, "radius": 0.09 * mm});
            skCircle(sketch, "E8.0.10.19", {"center": v(1.82, -1.13) * mm, "radius": 0.09 * mm});
            skCircle(sketch, "E8.2.10.19", {"center": v(2.04, -1.26) * mm, "radius": 0.09 * mm});
            skCircle(sketch, "E8.0.10.20", {"center": v(1.82, -1.36) * mm, "radius": 0.09 * mm});
            skCircle(sketch, "E8.0.10.21", {"center": v(1.82, -1.59) * mm, "radius": 0.09 * mm});
            skCircle(sketch, "E9.0.11.10", {"center": v(2.27, 0.91) * mm, "radius": 0.09 * mm});
            skCircle(sketch, "E9.0.11.11", {"center": v(2.27, 0.68) * mm, "radius": 0.09 * mm});
            skCircle(sketch, "E9.0.11.12", {"center": v(2.27, 0.46) * mm, "radius": 0.09 * mm});
            skCircle(sketch, "E9.0.11.13", {"center": v(2.27, 0.23) * mm, "radius": 0.09 * mm});
            skCircle(sketch, "E9.0.11.14", {"center": v(2.27, 0) * mm, "radius": 0.09 * mm});
            skCircle(sketch, "E9.0.11.15", {"center": v(2.27, -0.22) * mm, "radius": 0.09 * mm});
            skCircle(sketch, "E9.0.11.16", {"center": v(2.27, -0.45) * mm, "radius": 0.09 * mm});
            skCircle(sketch, "E9.0.11.17", {"center": v(2.27, -0.68) * mm, "radius": 0.09 * mm});
            skCircle(sketch, "E9.0.11.18", {"center": v(2.27, -0.9) * mm, "radius": 0.09 * mm});
            skCircle(sketch, "E10.0.3.22", {"center": v(-1.36, -1.81) * mm, "radius": 0.09 * mm});
            skCircle(sketch, "E10.2.3.22", {"center": v(-1.13, -1.94) * mm, "radius": 0.09 * mm});
            skCircle(sketch, "E10.0.3.23", {"center": v(-1.36, -2.04) * mm, "radius": 0.09 * mm});
            skCircle(sketch, "E10.2.3.23", {"center": v(-1.13, -2.17) * mm, "radius": 0.09 * mm});
            skCircle(sketch, "E10.0.4.22", {"center": v(-0.9, -1.81) * mm, "radius": 0.09 * mm});
            skCircle(sketch, "E10.2.4.22", {"center": v(-0.68, -1.94) * mm, "radius": 0.09 * mm});
            skCircle(sketch, "E10.0.4.23", {"center": v(-0.9, -2.04) * mm, "radius": 0.09 * mm});
            skCircle(sketch, "E10.2.4.23", {"center": v(-0.68, -2.17) * mm, "radius": 0.09 * mm});
            skCircle(sketch, "E10.0.4.24", {"center": v(-0.9, -2.27) * mm, "radius": 0.09 * mm});
            skCircle(sketch, "E10.0.5.22", {"center": v(-0.45, -1.81) * mm, "radius": 0.09 * mm});
            skCircle(sketch, "E10.2.5.22", {"center": v(-0.23, -1.94) * mm, "radius": 0.09 * mm});
            skCircle(sketch, "E10.0.5.23", {"center": v(-0.45, -2.04) * mm, "radius": 0.09 * mm});
            skCircle(sketch, "E10.2.5.23", {"center": v(-0.23, -2.17) * mm, "radius": 0.09 * mm});
            skCircle(sketch, "E10.0.5.24", {"center": v(-0.45, -2.27) * mm, "radius": 0.09 * mm});
            skCircle(sketch, "E10.2.5.24", {"center": v(-0.23, -2.4) * mm, "radius": 0.09 * mm});
            skCircle(sketch, "E10.0.6.22", {"center": v(0, -1.81) * mm, "radius": 0.09 * mm});
            skCircle(sketch, "E10.2.6.22", {"center": v(0.23, -1.94) * mm, "radius": 0.09 * mm});
            skCircle(sketch, "E10.0.6.23", {"center": v(0, -2.04) * mm, "radius": 0.09 * mm});
            skCircle(sketch, "E10.2.6.23", {"center": v(0.23, -2.17) * mm, "radius": 0.09 * mm});
            skCircle(sketch, "E10.0.6.24", {"center": v(0, -2.27) * mm, "radius": 0.09 * mm});
            skCircle(sketch, "E10.2.6.24", {"center": v(0.23, -2.4) * mm, "radius": 0.09 * mm});
            skCircle(sketch, "E10.0.7.22", {"center": v(0.45, -1.81) * mm, "radius": 0.09 * mm});
            skCircle(sketch, "E10.2.7.22", {"center": v(0.68, -1.94) * mm, "radius": 0.09 * mm});
            skCircle(sketch, "E10.0.7.23", {"center": v(0.45, -2.04) * mm, "radius": 0.09 * mm});
            skCircle(sketch, "E10.2.7.23", {"center": v(0.68, -2.17) * mm, "radius": 0.09 * mm});
            skCircle(sketch, "E10.0.7.24", {"center": v(0.45, -2.27) * mm, "radius": 0.09 * mm});
            skCircle(sketch, "E10.0.8.22", {"center": v(0.9, -1.81) * mm, "radius": 0.09 * mm});
            skCircle(sketch, "E10.2.8.22", {"center": v(1.14, -1.94) * mm, "radius": 0.09 * mm});
            skCircle(sketch, "E10.0.8.23", {"center": v(0.9, -2.04) * mm, "radius": 0.09 * mm});
            skCircle(sketch, "E10.2.8.23", {"center": v(1.14, -2.17) * mm, "radius": 0.09 * mm});
            skCircle(sketch, "E10.0.8.24", {"center": v(0.9, -2.27) * mm, "radius": 0.09 * mm});
            skCircle(sketch, "E10.0.9.22", {"center": v(1.36, -1.81) * mm, "radius": 0.09 * mm});
            skCircle(sketch, "E10.0.9.23", {"center": v(1.36, -2.04) * mm, "radius": 0.09 * mm});
            skCircle(sketch, "E11.0", {"center": v(0, 0) * mm, "radius": 2.5 * mm, "construction": true});
            skSolve(sketch);
        }
        {
            var Q0;
            Q0=qSketchRegion(id+"F3",true);
            extrude(context, id + "F4", {"entities" : qUnion([Q0]), "operationType" : NewBodyOperationType.REMOVE, "endBound" : BoundingType.THROUGH_ALL, "oppositeDirection" : true, "depth" : 25 * mm});
        }
    });
